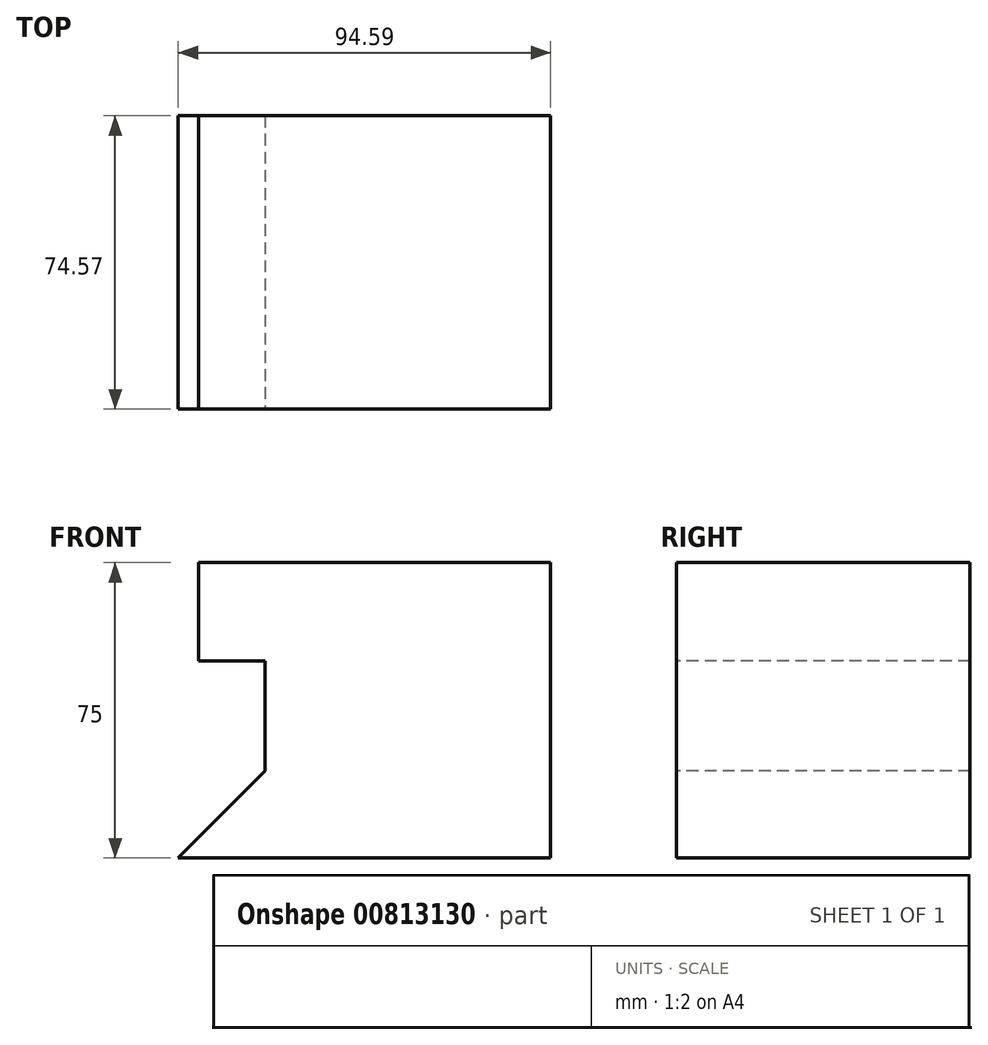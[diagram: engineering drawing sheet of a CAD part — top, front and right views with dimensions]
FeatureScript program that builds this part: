
annotation { "Feature Type Name" : "Feature", "Feature Type Description" : "" }
export const myFeature = defineFeature(function(context is Context, id is Id, definition is map)
    precondition{}
    {
        {
            var Q0;
            Q0=qCreatedBy(makeId("Top.planeOp"),FACE);
            var sketch = newSketch(context, id + "F0", { "sketchPlane" : qUnion([Q0])});
            skLineSegment(sketch, "E0.bottom", {"start": v(-51.62, 34.02) * mm, "end": v(57.97, 34.02) * mm});
            skLineSegment(sketch, "E0.top", {"start": v(-51.62, -40.55) * mm, "end": v(57.97, -40.55) * mm});
            skLineSegment(sketch, "E0.left", {"start": v(-51.62, 34.02) * mm, "end": v(-51.62, -40.55) * mm});
            skLineSegment(sketch, "E0.right", {"start": v(57.97, 34.02) * mm, "end": v(57.97, -40.55) * mm});
            skSolve(sketch);
        }
        {
            var Q0;
            Q0=makeQuery(id+"F0.imprint","IMPRINT",FACE,{"disambiguationData":[TD([[makeQuery(id+"F0.imprint","IMPRINT",EDGE,{"derivedFrom":sQuery(id+"F0.wireOp",EDGE,"E0.bottom")}),-1.0]])]});
            extrude(context, id + "F1", {"entities" : qUnion([Q0]), "depth" : 25 * mm, "offsetDistance" : 25 * mm});
        }
        {
            var Q0;
            Q0=makeQuery(id+"F1.opExtrude","CAP_FACE",FACE,{"disambiguationData":[OSD([sQuery(id+"F0.wireOp",EDGE,"E0.bottom"),sQuery(id+"F0.wireOp",EDGE,"E0.top"),sQuery(id+"F0.wireOp",EDGE,"E0.left"),sQuery(id+"F0.wireOp",EDGE,"E0.right")])],"isStart":false});
            var sketch = newSketch(context, id + "F2", { "sketchPlane" : qUnion([Q0])});
            skLineSegment(sketch, "E1.bottom", {"start": v(-14.58, 34.02) * mm, "end": v(57.97, 34.02) * mm});
            skLineSegment(sketch, "E1.top", {"start": v(-14.58, -40.55) * mm, "end": v(57.97, -40.55) * mm});
            skLineSegment(sketch, "E1.left", {"start": v(-14.58, 34.02) * mm, "end": v(-14.58, -40.55) * mm});
            skLineSegment(sketch, "E1.right", {"start": v(57.97, 34.02) * mm, "end": v(57.97, -40.55) * mm});
            skSolve(sketch);
        }
        {
            var Q0;
            Q0=makeQuery(id+"F2.imprint","IMPRINT",FACE,{"disambiguationData":[TD([[makeQuery(id+"F2.imprint","IMPRINT",EDGE,{"derivedFrom":sQuery(id+"F2.wireOp",EDGE,"E1.bottom")}),-1.0]])]});
            extrude(context, id + "F3", {"entities" : qUnion([Q0]), "operationType" : NewBodyOperationType.ADD, "depth" : 25 * mm, "offsetDistance" : 25 * mm});
        }
        {
            var Q0;
            Q0=makeQuery(id+"F3.opExtrude","CAP_FACE",FACE,{"disambiguationData":[OSD([sQuery(id+"F2.wireOp",EDGE,"E1.bottom"),sQuery(id+"F2.wireOp",EDGE,"E1.top"),sQuery(id+"F2.wireOp",EDGE,"E1.left"),sQuery(id+"F2.wireOp",EDGE,"E1.right")])],"isStart":false});
            var sketch = newSketch(context, id + "F4", { "sketchPlane" : qUnion([Q0])});
            skLineSegment(sketch, "E2.bottom", {"start": v(57.97, 34.02) * mm, "end": v(-31.48, 34.02) * mm});
            skLineSegment(sketch, "E2.top", {"start": v(57.97, -40.55) * mm, "end": v(-31.48, -40.55) * mm});
            skLineSegment(sketch, "E2.left", {"start": v(57.97, 34.02) * mm, "end": v(57.97, -40.55) * mm});
            skLineSegment(sketch, "E2.right", {"start": v(-31.48, 34.02) * mm, "end": v(-31.48, -40.55) * mm});
            skSolve(sketch);
        }
        {
            var Q0;
            {var subQ0=sQuery(id+"F4.wireOp",EDGE,"E2.left");Q0=makeQuery(id+"F4.imprint","IMPRINT",FACE,{"disambiguationData":[TD([[makeQuery(id+"F4.imprint","IMPRINT",EDGE,{"derivedFrom":subQ0}),-1.0]])]});}
            var Q1;
            {var subQ2=sQuery(id+"F4.wireOp",EDGE,"E2.right");Q1=makeQuery(id+"F4.imprint","IMPRINT",FACE,{"disambiguationData":[TD([[makeQuery(id+"F4.imprint","IMPRINT",EDGE,{"derivedFrom":subQ2}),1.0]])]});}
            extrude(context, id + "F5", {"entities" : qUnion([Q0, Q1]), "operationType" : NewBodyOperationType.ADD, "depth" : 25 * mm, "offsetDistance" : 25 * mm});
        }
        {
            var Q0;
            Q0=makeQuery(id+"F1.opExtrude","CAP_EDGE",EDGE,{"disambiguationData":[OSD([sQuery(id+"F0.wireOp",EDGE,"E0.left")])],"isStart":false});
            chamfer(context, id + "F6", {"entities" : qUnion([Q0]), "width" : 40 * mm, "tangentPropagation" : true});
        }
    });
